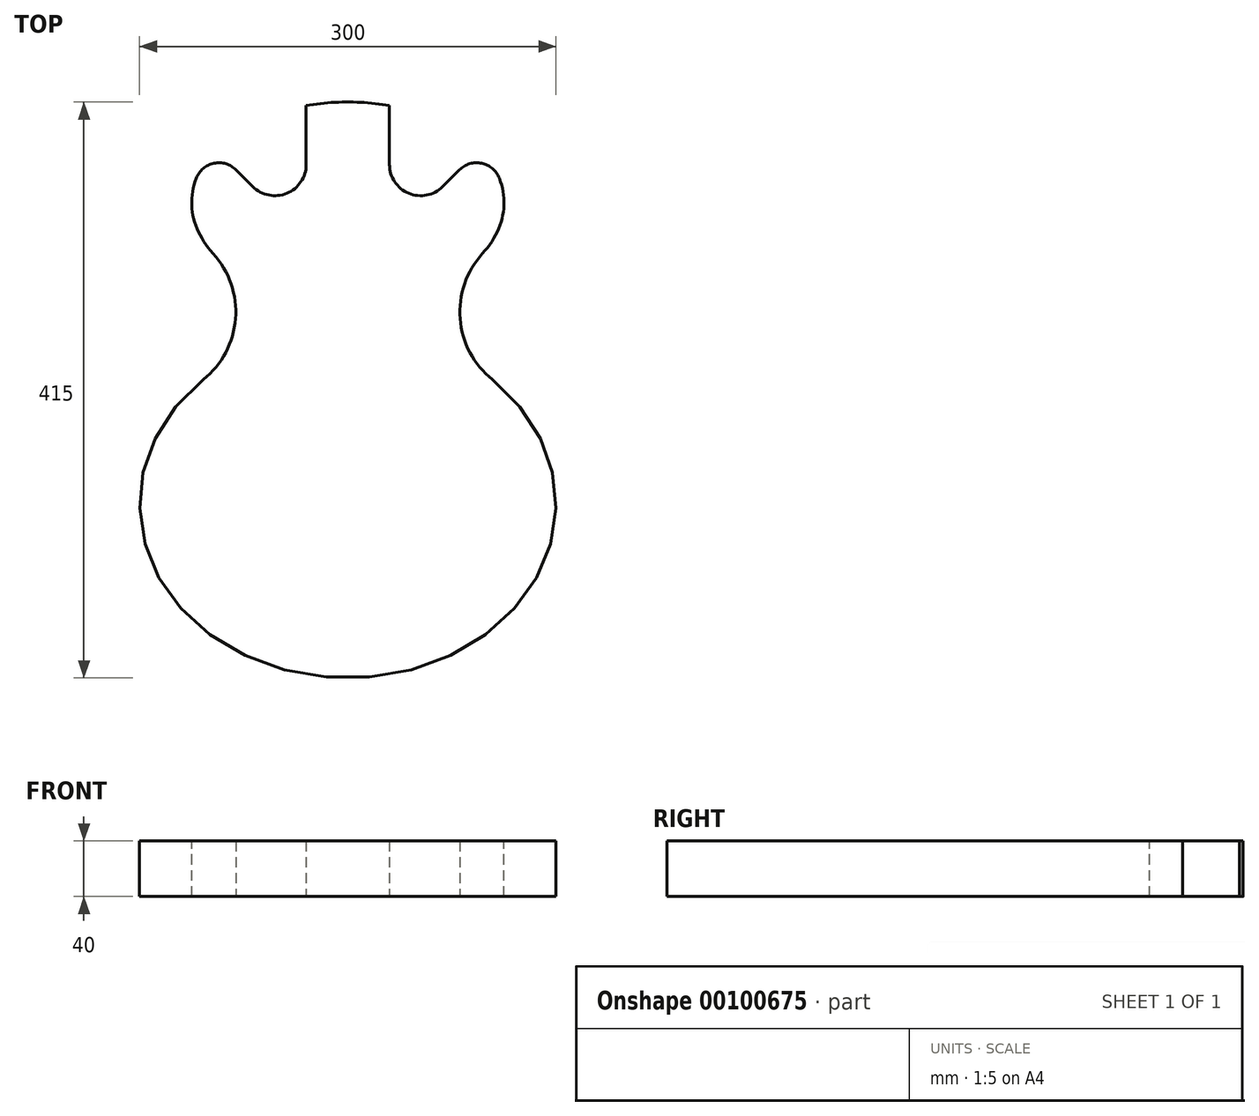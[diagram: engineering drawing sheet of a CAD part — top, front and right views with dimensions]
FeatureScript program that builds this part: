
annotation { "Feature Type Name" : "Feature", "Feature Type Description" : "" }
export const myFeature = defineFeature(function(context is Context, id is Id, definition is map)
    precondition{}
    {
        {
            var Q0;
            Q0=qCreatedBy(makeId("Top.planeOp"),FACE);
            var sketch = newSketch(context, id + "F0", { "sketchPlane" : qUnion([Q0])});
            skEllipticalArc(sketch, "E0", {});
            skEllipticalArc(sketch, "E1", {});
            skLineSegment(sketch, "E2", {"start": v(0, 0) * mm, "end": v(0, 415) * mm, "construction": true});
            skLineSegment(sketch, "E3", {"start": v(-244.22, 0) * mm, "end": v(-244.22, 277.4) * mm, "construction": true});
            skLineSegment(sketch, "E4", {"start": v(-244.22, 277.4) * mm, "end": v(0, 277.4) * mm, "construction": true});
            skLineSegment(sketch, "E5", {"start": v(33.04, 277.4) * mm, "end": v(-65.62, 237.4) * mm, "construction": true});
            skEllipticalArc(sketch, "E6.MirrorCS", {});
            skEllipticalArc(sketch, "E7.MirrorCS", {});
            skPoint(sketch, "E8.orphan", {"position": v(136.53, 345.4) * mm});
            skPoint(sketch, "E9.orphan", {"position": v(-136.53, 345.4) * mm});
            skLineSegment(sketch, "E10", {"start": v(-65.62, 237.4) * mm, "end": v(-65.62, 237.4) * mm});
            skLineSegment(sketch, "E11", {"start": v(65.62, 237.4) * mm, "end": v(65.62, 237.4) * mm});
            skPoint(sketch, "E12.MirrorCS.start.orphan", {"position": v(66.96, 284.24) * mm});
            skArc(sketch, "E13", {"start": v(-104.07, 215.02) * mm, "mid": v(-80.9, 258.87) * mm, "end": v(-97, 305.79) * mm});
            skPoint(sketch, "E14.center.orphan", {"position": v(-75.01, 260.57) * mm});
            skPoint(sketch, "E14.end.orphan", {"position": v(-66.96, 284.24) * mm});
            skArc(sketch, "E15.MirrorC", {"start": v(104.07, 215.02) * mm, "mid": v(80.9, 258.87) * mm, "end": v(97, 305.79) * mm});
            const initialGuessF0  = {"E0": [0, 0.125, 0, -1, 0.125, 0.15, 3.908375998079658, 6.283185307179586], "E1": [0, 0.3425, -1, 0, 0.1125, 0.0725, 4.71238898038469, 0.5309816561281908], "E6.MirrorCS": [0, 0.3425, 1, 0, 0.1125, 0.0725, 5.752203651051396, 1.5707963267948966], "E7.MirrorCS": [0, 0.125, 0, -1, 0.125, 0.15, 6.283185307179586, 2.3748093090999287]};
            skSetInitialGuess(sketch, initialGuessF0);
            skSolve(sketch);
        }
        {
            var Q0;
            Q0=qSketchRegion(id+"F0",true);
            extrude(context, id + "F1", {"entities" : qUnion([Q0]), "depth" : 40 * mm});
        }
        {
            var Q0;
            Q0=makeQuery(id+"F1.opExtrude","CAP_FACE",FACE,{"disambiguationData":[OSD([sQuery(id+"F0.wireOp",EDGE,"E0"),sQuery(id+"F0.wireOp",EDGE,"E1"),sQuery(id+"F0.wireOp",EDGE,"00a93f0c-93eb-48e1-ab57-afecb7497210"),sQuery(id+"F0.wireOp",EDGE,"E14"),sQuery(id+"F0.wireOp",EDGE,"E6.MirrorCS"),sQuery(id+"F0.wireOp",EDGE,"E12.MirrorCS"),sQuery(id+"F0.wireOp",EDGE,"a32407f8-8c26-4124-8342-763ddac0a0100.MirrorCS"),sQuery(id+"F0.wireOp",EDGE,"E7.MirrorCS"),sQuery(id+"F0.wireOp",EDGE,"E10"),sQuery(id+"F0.wireOp",EDGE,"E11")])],"isStart":false});
            var sketch = newSketch(context, id + "F2", { "sketchPlane" : qUnion([Q0])});
            skLineSegment(sketch, "E16", {"start": v(0, 415) * mm, "end": v(0, 350) * mm, "construction": true});
            skPoint(sketch, "E16.endSnap0", {"position": v(0, 415) * mm});
            skLineSegment(sketch, "E17.0", {"start": v(30, 415) * mm, "end": v(30, 370) * mm});
            skLineSegment(sketch, "E18", {"start": v(0, 415) * mm, "end": v(30, 415) * mm, "construction": true});
            skArc(sketch, "E19", {"start": v(30, 370) * mm, "mid": v(43.89, 349.21) * mm, "end": v(68.4, 354.1) * mm});
            skLineSegment(sketch, "E20", {"start": v(68.4, 354.1) * mm, "end": v(80.45, 366.13) * mm});
            skArc(sketch, "E21", {"start": v(109.14, 360.09) * mm, "mid": v(96.43, 370.88) * mm, "end": v(80.45, 366.13) * mm});
            skLineSegment(sketch, "E22", {"start": v(109.14, 360.09) * mm, "end": v(87.83, 415) * mm});
            skLineSegment(sketch, "E23", {"start": v(30, 415) * mm, "end": v(87.83, 415) * mm});
            skLineSegment(sketch, "E24.MirrorCS", {"start": v(-30, 415) * mm, "end": v(-30, 370) * mm});
            skArc(sketch, "E25.MirrorCS", {"start": v(-30, 370) * mm, "mid": v(-43.89, 349.21) * mm, "end": v(-68.4, 354.1) * mm});
            skLineSegment(sketch, "E26.MirrorCS", {"start": v(-68.4, 354.1) * mm, "end": v(-80.45, 366.13) * mm});
            skArc(sketch, "E27.MirrorCS", {"start": v(-109.14, 360.09) * mm, "mid": v(-96.43, 370.88) * mm, "end": v(-80.45, 366.13) * mm});
            skLineSegment(sketch, "E28.MirrorCS", {"start": v(-109.14, 360.09) * mm, "end": v(-87.83, 415) * mm});
            skLineSegment(sketch, "E29.MirrorCS", {"start": v(-30, 415) * mm, "end": v(-87.83, 415) * mm});
            skSolve(sketch);
        }
        {
            var Q0;
            Q0=qSketchRegion(id+"F2",true);
            extrude(context, id + "F3", {"entities" : qUnion([Q0]), "operationType" : NewBodyOperationType.REMOVE, "endBound" : BoundingType.THROUGH_ALL, "oppositeDirection" : true, "depth" : 25 * mm});
        }
    });
